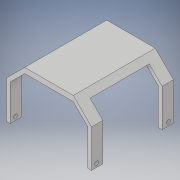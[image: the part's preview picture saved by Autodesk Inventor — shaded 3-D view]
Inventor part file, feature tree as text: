
AUTODESK INVENTOR PART (.ipt)
format: ipt  version: 2017 (Build 210142000, 142)  size: 161,280 bytes
history: native  units: in
note: dims shown in document units (in); Inventor stores cm internally (conversion verified against a paired STEP export)
features: sketch x4, projected_geometry x4, extrude x3, chamfer x1, hole x1
ambient origin geometry x8: Origin, YZ Plane, XZ Plane, XY Plane, X Axis, Y Axis, Z Axis, Center Point
bodies: Solid1 (feature_tree)
feature tree (13):
  extrude  "Extrusion1"  Depth=2.7in
  chamfer  "Chamfer1"  Distance=2.8in
  extrude  "Extrusion2"  Depth=0.125in
  hole  "Hole2"  [1 undecoded]
  extrude  "Extrusion3"  Depth=2.7in
  sketch  "Sketch1"  dims[d0=1.84in d1=2.7in d2=2.8in d3=0.0in]
  sketch  "Sketch2"  dims[d4=0.6in d5=0.125in d6=45.0deg d12=0.125in]
  projected_geometry  "Projected Loop1"
  sketch  "Sketch3"  dims[d13=0.125in d14=5.0in d15=0.0in]
  projected_geometry  "Projected Loop2"
  sketch  "Sketch4"  dims[d16=2.364in d17=2.7in d18=0.168in d19=0.63in d20=1.24in d21=0.125in d29=0.125in d30=0.75in d31=0.375in d32=0.25in d33=0.5635in d34=1.0in d35=0.8108in d36=0.125in d37=0.125in d38=0.125in d39=0.125in d40=1.6632in d41=2.7in d42=1.95in d43=0.375in d44=5.0in d45=0.0in]
  projected_geometry  "Projected Loop3"
  projected_geometry  "Projected Loop4"
note: 1 required parameter value undecoded (feature->parameter linkage not recoverable at this tier; creation-order binding heuristic only, values carry confidence <= 0.55)
